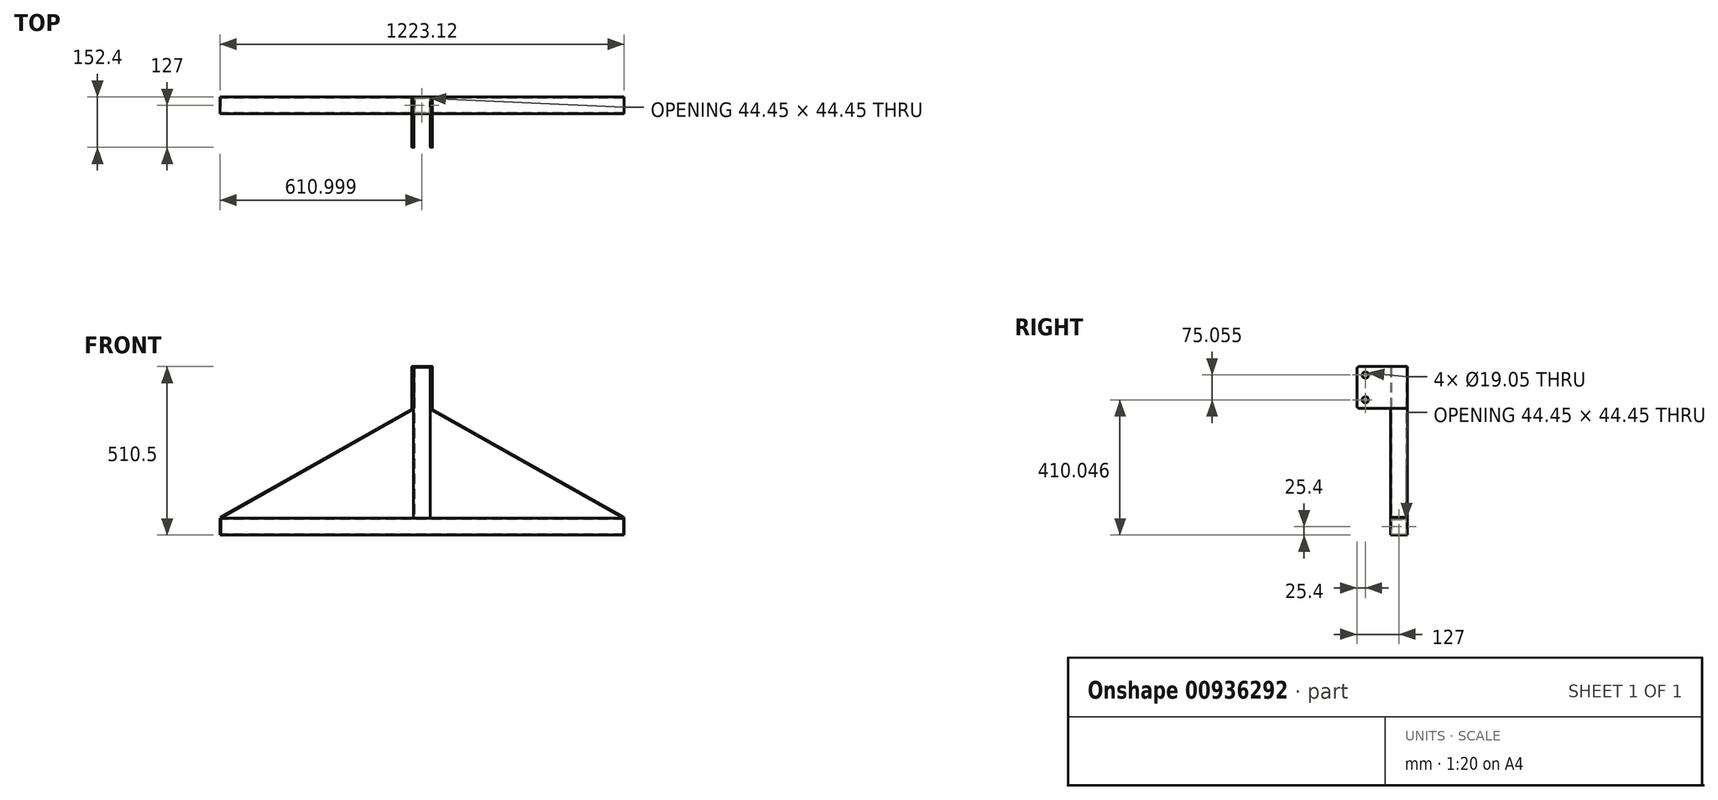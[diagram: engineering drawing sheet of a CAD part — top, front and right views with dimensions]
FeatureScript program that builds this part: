
annotation { "Feature Type Name" : "Feature", "Feature Type Description" : "" }
export const myFeature = defineFeature(function(context is Context, id is Id, definition is map)
    precondition{}
    {
        {
            var Q0;
            Q0=qCreatedBy(makeId("Right.planeOp"),FACE);
            var sketch = newSketch(context, id + "F0", { "sketchPlane" : qUnion([Q0])});
            skLineSegment(sketch, "E0.bottom", {"start": v(-48.26, 50.8) * mm, "end": v(-2.54, 50.8) * mm});
            skLineSegment(sketch, "E0.top", {"start": v(-48.26, 0) * mm, "end": v(-2.54, 0) * mm});
            skLineSegment(sketch, "E0.left", {"start": v(-50.8, 48.26) * mm, "end": v(-50.8, 2.54) * mm});
            skLineSegment(sketch, "E0.right", {"start": v(0, 48.26) * mm, "end": v(0, 2.54) * mm});
            skPoint(sketch, "E1.visualSharp", {"position": v(-50.8, 50.8) * mm});
            skArc(sketch, "E1.filletArc", {"start": v(-48.26, 50.8) * mm, "mid": v(-50.06, 50.06) * mm, "end": v(-50.8, 48.26) * mm});
            skPoint(sketch, "E2.visualSharp", {"position": v(0, 50.8) * mm});
            skArc(sketch, "E2.filletArc", {"start": v(0, 48.26) * mm, "mid": v(-0.74, 50.06) * mm, "end": v(-2.54, 50.8) * mm});
            skPoint(sketch, "E3.visualSharp", {"position": v(0, 0) * mm});
            skArc(sketch, "E3.filletArc", {"start": v(-2.54, 0) * mm, "mid": v(-0.74, 0.74) * mm, "end": v(0, 2.54) * mm});
            skPoint(sketch, "E4.visualSharp", {"position": v(-50.8, 0) * mm});
            skArc(sketch, "E4.filletArc", {"start": v(-50.8, 2.54) * mm, "mid": v(-50.06, 0.74) * mm, "end": v(-48.26, 0) * mm});
            skLineSegment(sketch, "E5.1", {"start": v(-45.09, 47.62) * mm, "end": v(-5.72, 47.62) * mm});
            skLineSegment(sketch, "E5.2", {"start": v(-47.63, 45.09) * mm, "end": v(-47.63, 5.71) * mm});
            skLineSegment(sketch, "E5.5", {"start": v(-45.09, 3.17) * mm, "end": v(-5.71, 3.17) * mm});
            skLineSegment(sketch, "E5.7", {"start": v(-3.18, 45.09) * mm, "end": v(-3.17, 5.71) * mm});
            skArc(sketch, "E6.filletArc", {"start": v(-45.09, 47.62) * mm, "mid": v(-46.88, 46.88) * mm, "end": v(-47.63, 45.09) * mm});
            skArc(sketch, "E7.filletArc", {"start": v(-3.17, 45.09) * mm, "mid": v(-3.92, 46.88) * mm, "end": v(-5.72, 47.62) * mm});
            skArc(sketch, "E8.filletArc", {"start": v(-5.71, 3.17) * mm, "mid": v(-3.92, 3.92) * mm, "end": v(-3.17, 5.71) * mm});
            skArc(sketch, "E9.filletArc", {"start": v(-47.63, 5.71) * mm, "mid": v(-46.88, 3.92) * mm, "end": v(-45.09, 3.17) * mm});
            skSolve(sketch);
        }
        {
            var Q0;
            Q0=makeQuery(id+"F0.imprint","IMPRINT",FACE,{"disambiguationData":[TD([[makeQuery(id+"F0.imprint","IMPRINT",EDGE,{"derivedFrom":sQuery(id+"F0.wireOp",EDGE,"E0.bottom")}),-1.0]])]});
            extrude(context, id + "F1", {"entities" : qUnion([Q0]), "endBound" : BoundingType.SYMMETRIC, "depth" : 1219.2 * mm, "offsetDistance" : 25.4 * mm});
        }
        {
            var Q0;
            Q0=makeQuery(id+"F1.opExtrude","SWEPT_FACE",FACE,{"disambiguationData":[OSD([sQuery(id+"F0.wireOp",EDGE,"E0.bottom")])]});
            var sketch = newSketch(context, id + "F2", { "sketchPlane" : qUnion([Q0])});
            skLineSegment(sketch, "E10.bottom", {"start": v(-23.42, 0) * mm, "end": v(22.3, 0) * mm});
            skLineSegment(sketch, "E10.top", {"start": v(-23.42, -50.8) * mm, "end": v(22.3, -50.8) * mm});
            skLineSegment(sketch, "E10.left", {"start": v(-25.96, -2.54) * mm, "end": v(-25.96, -48.26) * mm});
            skLineSegment(sketch, "E10.right", {"start": v(24.84, -2.54) * mm, "end": v(24.84, -48.26) * mm});
            skLineSegment(sketch, "E11.0", {"start": v(-22.79, -5.72) * mm, "end": v(-22.79, -45.09) * mm});
            skLineSegment(sketch, "E11.1", {"start": v(-20.25, -3.18) * mm, "end": v(19.12, -3.18) * mm});
            skLineSegment(sketch, "E11.2", {"start": v(21.66, -5.72) * mm, "end": v(21.66, -45.09) * mm});
            skLineSegment(sketch, "E11.3", {"start": v(-20.25, -47.63) * mm, "end": v(19.12, -47.63) * mm});
            skPoint(sketch, "E12.visualSharp", {"position": v(-25.96, 0) * mm});
            skArc(sketch, "E12.filletArc", {"start": v(-23.42, 0) * mm, "mid": v(-25.22, -0.74) * mm, "end": v(-25.96, -2.54) * mm});
            skPoint(sketch, "E13.visualSharp", {"position": v(24.84, 0) * mm});
            skArc(sketch, "E13.filletArc", {"start": v(24.84, -2.54) * mm, "mid": v(24.1, -0.74) * mm, "end": v(22.3, 0) * mm});
            skPoint(sketch, "E14.visualSharp", {"position": v(21.66, -3.18) * mm});
            skArc(sketch, "E14.filletArc", {"start": v(21.66, -5.72) * mm, "mid": v(20.92, -3.92) * mm, "end": v(19.12, -3.18) * mm});
            skPoint(sketch, "E15.visualSharp", {"position": v(21.66, -47.63) * mm});
            skArc(sketch, "E15.filletArc", {"start": v(19.12, -47.63) * mm, "mid": v(20.92, -46.88) * mm, "end": v(21.66, -45.09) * mm});
            skPoint(sketch, "E16.visualSharp", {"position": v(24.84, -50.8) * mm});
            skArc(sketch, "E16.filletArc", {"start": v(22.3, -50.8) * mm, "mid": v(24.1, -50.06) * mm, "end": v(24.84, -48.26) * mm});
            skPoint(sketch, "E17.visualSharp", {"position": v(-22.79, -47.63) * mm});
            skArc(sketch, "E17.filletArc", {"start": v(-22.79, -45.09) * mm, "mid": v(-22.04, -46.88) * mm, "end": v(-20.25, -47.63) * mm});
            skPoint(sketch, "E18.visualSharp", {"position": v(-25.96, -50.8) * mm});
            skArc(sketch, "E18.filletArc", {"start": v(-25.96, -48.26) * mm, "mid": v(-25.22, -50.06) * mm, "end": v(-23.42, -50.8) * mm});
            skPoint(sketch, "E19.visualSharp", {"position": v(-22.79, -3.18) * mm});
            skArc(sketch, "E19.filletArc", {"start": v(-20.25, -3.18) * mm, "mid": v(-22.04, -3.92) * mm, "end": v(-22.79, -5.72) * mm});
            skSolve(sketch);
        }
        {
            var Q0;
            {var subQ0=sQuery(id+"F2.wireOp",EDGE,"E10.left");Q0=makeQuery(id+"F2.imprint","IMPRINT",FACE,{"disambiguationData":[TD([[makeQuery(id+"F2.imprint","IMPRINT",EDGE,{"derivedFrom":subQ0}),1.0]])]});}
            var Q1;
            Q1=makeQuery(id+"F2.imprint","IMPRINT",FACE,{"disambiguationData":[TD([[makeQuery(id+"F2.imprint","IMPRINT",EDGE,{"derivedFrom":sQuery(id+"F2.wireOp",EDGE,"E10.top")}),1.0]])]});
            var Q2;
            Q2=makeQuery(id+"F2.imprint","IMPRINT",FACE,{"disambiguationData":[TD([[makeQuery(id+"F2.imprint","IMPRINT",EDGE,{"derivedFrom":sQuery(id+"F2.wireOp",EDGE,"E10.bottom")}),-1.0]])]});
            extrude(context, id + "F3", {"entities" : qUnion([Q0, Q1, Q2]), "depth" : 457.2 * mm, "offsetDistance" : 25.4 * mm});
        }
        {
            var Q0;
            Q0=makeQuery(id+"F1.opExtrude","SWEPT_FACE",FACE,{"disambiguationData":[OSD([sQuery(id+"F0.wireOp",EDGE,"E0.left")])]});
            var sketch = newSketch(context, id + "F4", { "sketchPlane" : qUnion([Q0])});
            skLineSegment(sketch, "E20.0", {"start": v(609.6, 0) * mm, "end": v(-609.6, 0) * mm});
            skLineSegment(sketch, "E21.0", {"start": v(609.6, 50.8) * mm, "end": v(-609.6, 50.8) * mm});
            skLineSegment(sketch, "E22.0", {"start": v(-609.6, 48.26) * mm, "end": v(-609.6, 2.54) * mm});
            skPoint(sketch, "E23.0", {"position": v(-0.56, 508) * mm});
            skLineSegment(sketch, "E24.0", {"start": v(-23.42, 508) * mm, "end": v(22.3, 508) * mm});
            skLineSegment(sketch, "E25.0", {"start": v(609.6, 45.08) * mm, "end": v(609.6, 5.71) * mm});
            skPoint(sketch, "E26.0", {"position": v(-25.96, 508) * mm});
            skPoint(sketch, "E27.0", {"position": v(24.84, 508) * mm});
            skLineSegment(sketch, "E28.bottom", {"start": v(-25.96, 508) * mm, "end": v(24.84, 508) * mm});
            skLineSegment(sketch, "E28.top", {"start": v(-25.96, 510.5) * mm, "end": v(24.84, 510.5) * mm});
            skLineSegment(sketch, "E28.left", {"start": v(-25.96, 508) * mm, "end": v(-25.96, 510.5) * mm});
            skLineSegment(sketch, "E28.right", {"start": v(24.84, 508) * mm, "end": v(24.84, 510.5) * mm});
            skLineSegment(sketch, "E29", {"start": v(-27.92, 510.5) * mm, "end": v(-25.96, 510.5) * mm});
            skLineSegment(sketch, "E30", {"start": v(26.8, 510.5) * mm, "end": v(24.84, 510.5) * mm});
            skLineSegment(sketch, "E31.bottom", {"start": v(-609.6, 0) * mm, "end": v(-611.56, 0) * mm});
            skLineSegment(sketch, "E31.top", {"start": v(-609.6, 50.8) * mm, "end": v(-611.56, 50.8) * mm});
            skLineSegment(sketch, "E31.left", {"start": v(-609.6, 0) * mm, "end": v(-609.6, 50.8) * mm});
            skLineSegment(sketch, "E31.right", {"start": v(-611.56, 0) * mm, "end": v(-611.56, 50.8) * mm});
            skLineSegment(sketch, "E32.bottom", {"start": v(609.6, 0) * mm, "end": v(611.56, 0) * mm});
            skLineSegment(sketch, "E32.top", {"start": v(609.6, 50.8) * mm, "end": v(611.56, 50.8) * mm});
            skLineSegment(sketch, "E32.left", {"start": v(609.6, 0) * mm, "end": v(609.6, 50.8) * mm});
            skLineSegment(sketch, "E32.right", {"start": v(611.56, 0) * mm, "end": v(611.56, 50.8) * mm});
            skLineSegment(sketch, "E33", {"start": v(0, 0) * mm, "end": v(-0.56, 381) * mm, "construction": true});
            skLineSegment(sketch, "E34.0", {"start": v(-25.96, 508) * mm, "end": v(-25.96, 50.8) * mm});
            skLineSegment(sketch, "E35.0", {"start": v(24.84, 508) * mm, "end": v(24.84, 50.8) * mm});
            skLineSegment(sketch, "E36", {"start": v(-25.96, 381) * mm, "end": v(-609.6, 50.8) * mm});
            skLineSegment(sketch, "E37", {"start": v(24.84, 381) * mm, "end": v(609.6, 50.8) * mm});
            skLineSegment(sketch, "E38.0", {"start": v(-27.52, 383.76) * mm, "end": v(-611.16, 53.57) * mm});
            skLineSegment(sketch, "E39", {"start": v(-611.56, 50.8) * mm, "end": v(-611.56, 53.34) * mm});
            skLineSegment(sketch, "E40", {"start": v(-611.16, 53.57) * mm, "end": v(-611.56, 53.34) * mm});
            skPoint(sketch, "E41.orphan", {"position": v(-611.56, 53.57) * mm});
            skLineSegment(sketch, "E42", {"start": v(-611.56, 53.34) * mm, "end": v(-609.6, 50.8) * mm});
            skLineSegment(sketch, "E43", {"start": v(-27.52, 383.76) * mm, "end": v(-25.96, 384.65) * mm});
            skLineSegment(sketch, "E44.0", {"start": v(26.4, 383.76) * mm, "end": v(611.16, 53.56) * mm});
            skLineSegment(sketch, "E45", {"start": v(26.4, 383.76) * mm, "end": v(24.84, 384.65) * mm});
            skLineSegment(sketch, "E46", {"start": v(611.56, 50.8) * mm, "end": v(611.56, 53.34) * mm});
            skLineSegment(sketch, "E47", {"start": v(611.16, 53.56) * mm, "end": v(611.56, 53.34) * mm});
            skPoint(sketch, "E48.orphan", {"position": v(611.56, 53.56) * mm});
            skSolve(sketch);
        }
        {
            var Q0;
            {var subQ6=sQuery(id+"F4.wireOp",EDGE,"E32.bottom");Q0=makeQuery(id+"F4.imprint","IMPRINT",FACE,{"disambiguationData":[TD([[makeQuery(id+"F4.imprint","IMPRINT",EDGE,{"derivedFrom":subQ6}),1.0]])]});}
            var Q1;
            {var subQ3=sQuery(id+"F4.wireOp",EDGE,"E31.bottom");Q1=makeQuery(id+"F4.imprint","IMPRINT",FACE,{"disambiguationData":[TD([[makeQuery(id+"F4.imprint","IMPRINT",EDGE,{"derivedFrom":subQ3}),-1.0]])]});}
            var Q2;
            Q2=makeQuery(id+"F4.imprint","IMPRINT",FACE,{"disambiguationData":[TD([[makeQuery(id+"F4.imprint","IMPRINT",EDGE,{"derivedFrom":sQuery(id+"F4.wireOp",EDGE,"E28.top")}),-1.0]])]});
            var Q3;
            Q3=makeQuery(id+"F3.opExtrude","SWEPT_FACE",FACE,{"disambiguationData":[OSD([sQuery(id+"F2.wireOp",EDGE,"E10.bottom")])]});
            extrude(context, id + "F5", {"entities" : qUnion([Q0, Q1, Q2]), "endBound" : BoundingType.UP_TO_SURFACE, "oppositeDirection" : true, "depth" : 25.4 * mm, "endBoundEntityFace" : qUnion([Q3]), "offsetDistance" : 25.4 * mm});
        }
        {
            var Q0;
            {var subQ0=sQuery(id+"F4.wireOp",EDGE,"E36");Q0=makeQuery(id+"F4.imprint","IMPRINT",FACE,{"disambiguationData":[TD([[makeQuery(id+"F4.imprint","IMPRINT",EDGE,{"derivedFrom":subQ0}),-1.0]])]});}
            var Q1;
            Q1=makeQuery(id+"F4.imprint","IMPRINT",FACE,{"disambiguationData":[TD([[makeQuery(id+"F4.imprint","IMPRINT",EDGE,{"derivedFrom":sQuery(id+"F4.wireOp",EDGE,"E32.top")}),1.0]])]});
            var Q2;
            Q2=makeQuery(id+"F1.opExtrude","SWEPT_FACE",FACE,{"disambiguationData":[OSD([sQuery(id+"F0.wireOp",EDGE,"E0.right")])]});
            extrude(context, id + "F6", {"entities" : qUnion([Q0, Q1]), "endBound" : BoundingType.UP_TO_SURFACE, "oppositeDirection" : true, "depth" : 25.4 * mm, "endBoundEntityFace" : qUnion([Q2]), "offsetDistance" : 25.4 * mm});
        }
        {
            var Q0;
            Q0=makeQuery(id+"F3.opExtrude","SWEPT_FACE",FACE,{"disambiguationData":[OSD([sQuery(id+"F2.wireOp",EDGE,"E10.right")])]});
            var sketch = newSketch(context, id + "F7", { "sketchPlane" : qUnion([Q0])});
            skLineSegment(sketch, "E49.0", {"start": v(-50.8, 508) * mm, "end": v(-50.8, 50.8) * mm});
            skLineSegment(sketch, "E50.0", {"start": v(0, 508) * mm, "end": v(0, 50.8) * mm});
            skLineSegment(sketch, "E51.0", {"start": v(0, 510.5) * mm, "end": v(-50.8, 510.5) * mm});
            skLineSegment(sketch, "E52.0", {"start": v(0, 384.65) * mm, "end": v(-50.8, 384.65) * mm});
            skLineSegment(sketch, "E53.bottom", {"start": v(0, 510.5) * mm, "end": v(-146.05, 510.5) * mm});
            skLineSegment(sketch, "E53.top", {"start": v(0, 384.65) * mm, "end": v(-146.05, 384.65) * mm});
            skLineSegment(sketch, "E53.left", {"start": v(0, 510.5) * mm, "end": v(0, 384.65) * mm});
            skLineSegment(sketch, "E53.right", {"start": v(-152.4, 504.15) * mm, "end": v(-152.4, 391) * mm});
            skCircle(sketch, "E54", {"center": v(-127, 410.05) * mm, "radius": 9.53 * mm});
            skCircle(sketch, "E55", {"center": v(-127, 485.1) * mm, "radius": 9.53 * mm});
            skPoint(sketch, "E56.visualSharp", {"position": v(-152.4, 510.5) * mm});
            skArc(sketch, "E56.filletArc", {"start": v(-146.05, 510.5) * mm, "mid": v(-150.54, 508.64) * mm, "end": v(-152.4, 504.15) * mm});
            skPoint(sketch, "E57.visualSharp", {"position": v(-152.4, 384.65) * mm});
            skArc(sketch, "E57.filletArc", {"start": v(-152.4, 391) * mm, "mid": v(-150.54, 386.5) * mm, "end": v(-146.05, 384.65) * mm});
            skSolve(sketch);
        }
        {
            var Q0;
            Q0=makeQuery(id+"F7.imprint","IMPRINT",FACE,{"disambiguationData":[TD([[makeQuery(id+"F7.imprint","IMPRINT",EDGE,{"derivedFrom":sQuery(id+"F7.wireOp",EDGE,"E53.right")}),1.0]])]});
            var Q1;
            {var subQ1=sQuery(id+"F2.wireOp",EDGE,"E10.right");var subQ7=makeQuery(id+"F3.opExtrude","CAP_EDGE",EDGE,{"disambiguationData":[OSD([subQ1])],"isStart":false});Q1=makeQuery(id+"F7.imprint","IMPRINT",FACE,{"disambiguationData":[TD([[makeQuery(id+"F7.imprint","IMPRINT",EDGE,{"derivedFrom":subQ7}),1.0]])]});}
            extrude(context, id + "F8", {"entities" : qUnion([Q0, Q1]), "depth" : 6.35 * mm, "offsetDistance" : 25.4 * mm});
        }
        {
            var Q0;
            Q0=makeQuery(id+"F8.opExtrude","SWEPT_BODY",BODY,{"disambiguationData":[OSD([sQuery(id+"F7.wireOp",EDGE,"E53.bottom"),sQuery(id+"F7.wireOp",EDGE,"E53.top"),sQuery(id+"F7.wireOp",EDGE,"E53.left"),sQuery(id+"F7.wireOp",EDGE,"E53.right"),sQuery(id+"F7.wireOp",EDGE,"E54"),sQuery(id+"F7.wireOp",EDGE,"E55"),sQuery(id+"F7.wireOp",EDGE,"E56.filletArc"),sQuery(id+"F7.wireOp",EDGE,"E57.filletArc")])]});
            var Q1;
            Q1=qCreatedBy(makeId("Right.planeOp"),FACE);
            mirror(context, id + "F9", {"entities" : qUnion([Q0]), "mirrorPlane" : qUnion([Q1])});
        }
    });
